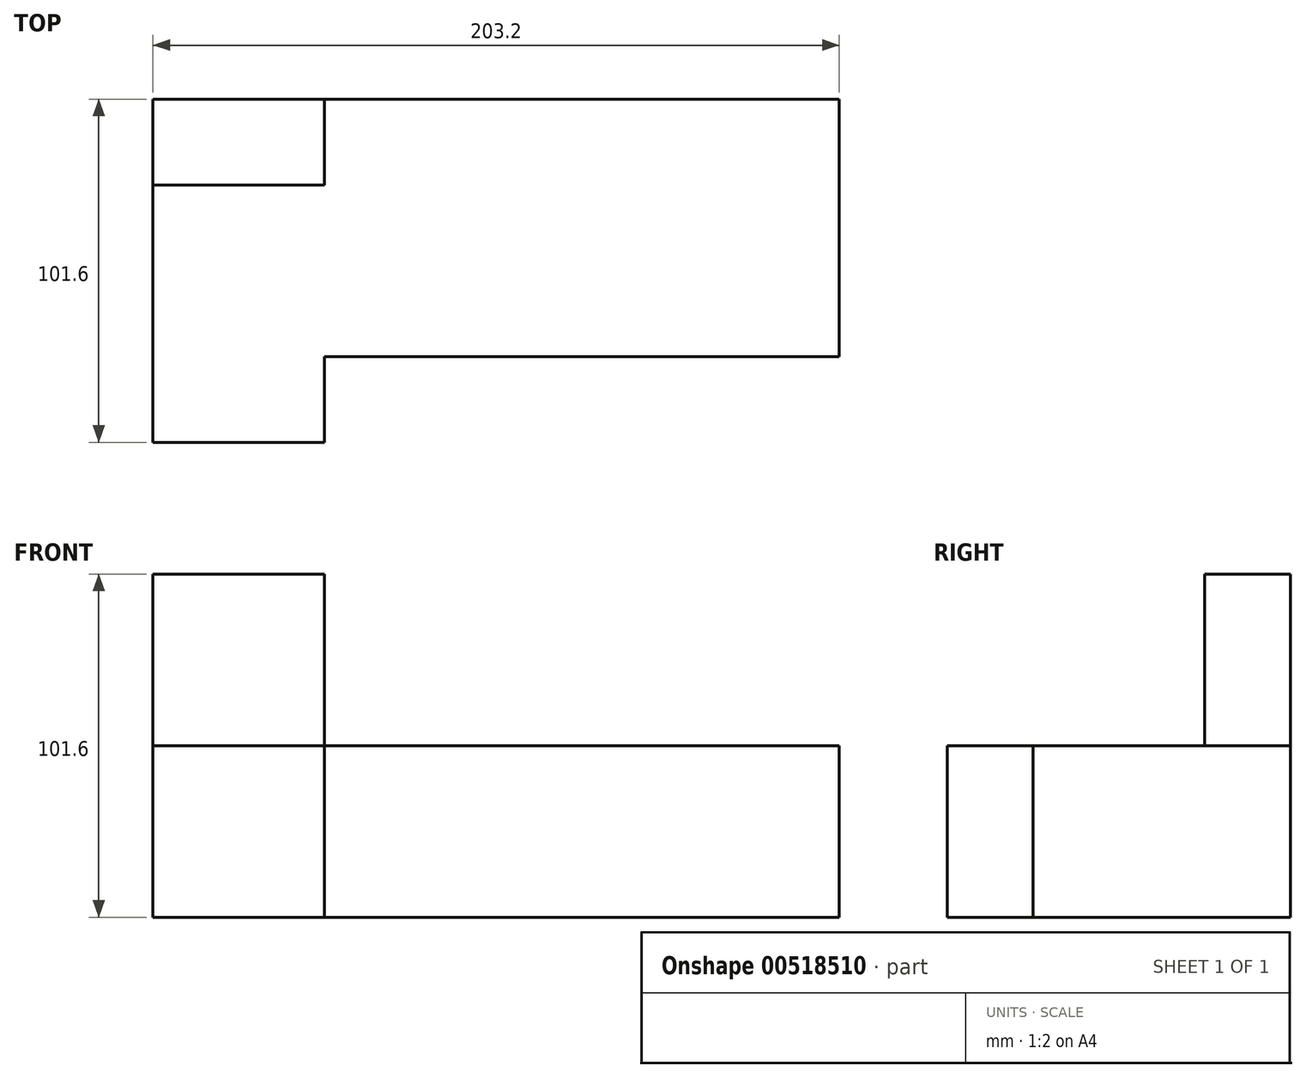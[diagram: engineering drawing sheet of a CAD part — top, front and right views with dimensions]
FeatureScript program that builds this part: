
annotation { "Feature Type Name" : "Feature", "Feature Type Description" : "" }
export const myFeature = defineFeature(function(context is Context, id is Id, definition is map)
    precondition{}
    {
        {
            var Q0;
            Q0=qCreatedBy(makeId("Front.planeOp"),FACE);
            var sketch = newSketch(context, id + "F0", { "sketchPlane" : qUnion([Q0])});
            skLineSegment(sketch, "E0.bottom", {"start": v(-143.3, -6.18) * mm, "end": v(59.9, -6.18) * mm});
            skLineSegment(sketch, "E0.top", {"start": v(-143.3, -56.98) * mm, "end": v(59.9, -56.98) * mm});
            skLineSegment(sketch, "E0.left", {"start": v(-143.3, -6.18) * mm, "end": v(-143.3, -56.98) * mm});
            skLineSegment(sketch, "E0.right", {"start": v(59.9, -6.18) * mm, "end": v(59.9, -56.98) * mm});
            skSolve(sketch);
        }
        {
            var Q0;
            Q0=qSketchRegion(id+"F0",true);
            extrude(context, id + "F1", {"entities" : qUnion([Q0]), "depth" : 101.6 * mm});
        }
        {
            var Q0;
            Q0=makeQuery(id+"F1.opExtrude","SWEPT_FACE",FACE,{"disambiguationData":[OSD([sQuery(id+"F0.wireOp",EDGE,"E0.bottom")])]});
            var sketch = newSketch(context, id + "F2", { "sketchPlane" : qUnion([Q0])});
            skLineSegment(sketch, "E1.bottom", {"start": v(59.9, -101.6) * mm, "end": v(-92.5, -101.6) * mm});
            skLineSegment(sketch, "E1.top", {"start": v(59.9, -76.2) * mm, "end": v(-92.5, -76.2) * mm});
            skLineSegment(sketch, "E1.left", {"start": v(59.9, -101.6) * mm, "end": v(59.9, -76.2) * mm});
            skLineSegment(sketch, "E1.right", {"start": v(-92.5, -101.6) * mm, "end": v(-92.5, -76.2) * mm});
            skSolve(sketch);
        }
        {
            var Q0;
            Q0=qSketchRegion(id+"F2",true);
            extrude(context, id + "F3", {"entities" : qUnion([Q0]), "operationType" : NewBodyOperationType.REMOVE, "endBound" : BoundingType.THROUGH_ALL, "oppositeDirection" : true, "depth" : -50.8 * mm});
        }
        {
            var Q0;
            Q0=makeQuery(id+"F1.opExtrude","SWEPT_FACE",FACE,{"disambiguationData":[OSD([sQuery(id+"F0.wireOp",EDGE,"E0.bottom")])]});
            var sketch = newSketch(context, id + "F4", { "sketchPlane" : qUnion([Q0])});
            skLineSegment(sketch, "E2.bottom", {"start": v(-143.3, 0) * mm, "end": v(-92.5, 0) * mm});
            skLineSegment(sketch, "E2.top", {"start": v(-143.3, -25.4) * mm, "end": v(-92.5, -25.4) * mm});
            skLineSegment(sketch, "E2.left", {"start": v(-143.3, 0) * mm, "end": v(-143.3, -25.4) * mm});
            skLineSegment(sketch, "E2.right", {"start": v(-92.5, 0) * mm, "end": v(-92.5, -25.4) * mm});
            skSolve(sketch);
        }
        {
            var Q0;
            Q0=qSketchRegion(id+"F4",true);
            extrude(context, id + "F5", {"entities" : qUnion([Q0]), "operationType" : NewBodyOperationType.ADD, "depth" : 50.8 * mm});
        }
    });
